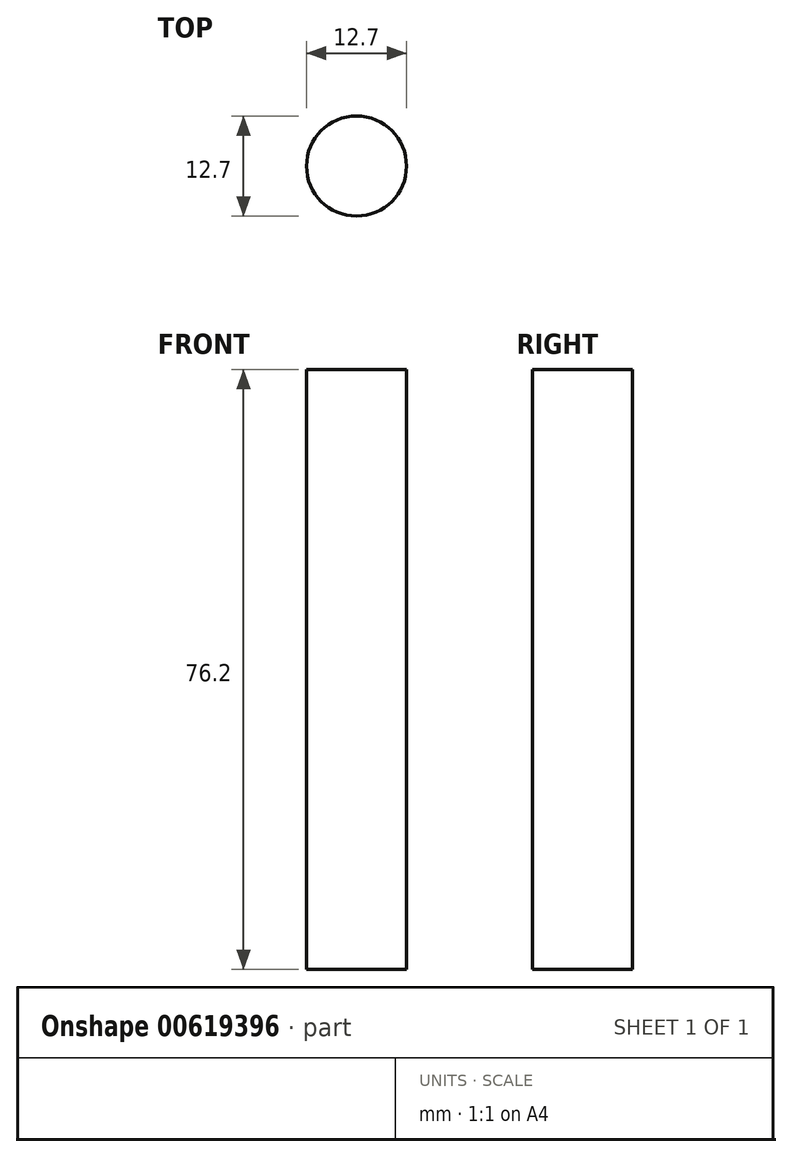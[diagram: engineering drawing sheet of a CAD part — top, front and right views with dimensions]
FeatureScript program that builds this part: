
annotation { "Feature Type Name" : "Feature", "Feature Type Description" : "" }
export const myFeature = defineFeature(function(context is Context, id is Id, definition is map)
    precondition{}
    {
        {
            var Q0;
            Q0=qCreatedBy(makeId("Front.planeOp"),FACE);
            var sketch = newSketch(context, id + "F0", { "sketchPlane" : qUnion([Q0])});
            skLineSegment(sketch, "E0.bottom", {"start": v(0, 0) * mm, "end": v(6.35, 0) * mm});
            skLineSegment(sketch, "E0.top", {"start": v(0, 76.2) * mm, "end": v(6.35, 76.2) * mm});
            skLineSegment(sketch, "E0.left", {"start": v(0, 0) * mm, "end": v(0, 76.2) * mm});
            skLineSegment(sketch, "E0.right", {"start": v(6.35, 0) * mm, "end": v(6.35, 76.2) * mm});
            skSolve(sketch);
        }
        {
            var Q0;
            Q0=makeQuery(id+"F0.imprint","IMPRINT",FACE,{"disambiguationData":[TD([[makeQuery(id+"F0.imprint","IMPRINT",EDGE,{"derivedFrom":sQuery(id+"F0.wireOp",EDGE,"E0.bottom")}),1.0]])]});
            var Q1;
            Q1=sQuery(id+"F0.wireOp",EDGE,"E0.left");
            revolve(context, id + "F1", {"entities" : qUnion([Q0]), "axis" : qUnion([Q1]), "revolveType" : RevolveType.FULL});
        }
    });
